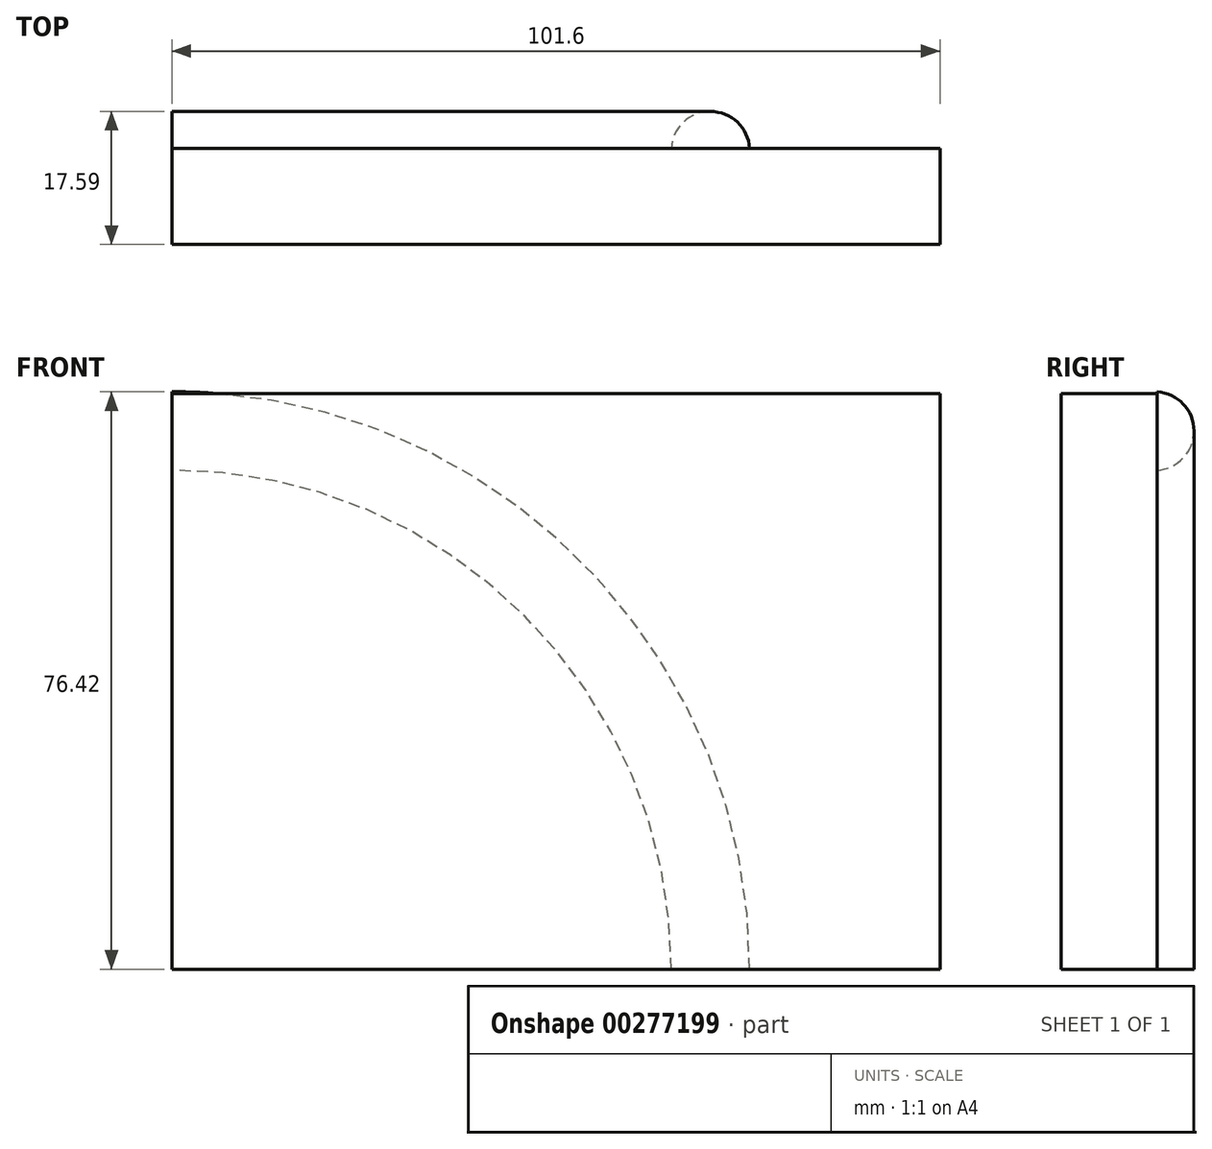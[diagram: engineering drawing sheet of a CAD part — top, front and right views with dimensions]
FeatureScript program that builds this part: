
annotation { "Feature Type Name" : "Feature", "Feature Type Description" : "" }
export const myFeature = defineFeature(function(context is Context, id is Id, definition is map)
    precondition{}
    {
        {
            var Q0;
            Q0=qCreatedBy(makeId("Front.planeOp"),FACE);
            var sketch = newSketch(context, id + "F0", { "sketchPlane" : qUnion([Q0])});
            skLineSegment(sketch, "E0.bottom", {"start": v(0, 0) * mm, "end": v(101.6, 0) * mm});
            skLineSegment(sketch, "E0.top", {"start": v(0, 76.2) * mm, "end": v(101.6, 76.2) * mm});
            skLineSegment(sketch, "E0.left", {"start": v(0, 0) * mm, "end": v(0, 76.2) * mm});
            skLineSegment(sketch, "E0.right", {"start": v(101.6, 0) * mm, "end": v(101.6, 76.2) * mm});
            skArc(sketch, "E1", {"start": v(0, 76.2) * mm, "mid": v(53.88, 53.88) * mm, "end": v(76.2, 0) * mm});
            skArc(sketch, "E2", {"start": v(71.12, 0) * mm, "mid": v(76.2, 5.08) * mm, "end": v(81.28, 0) * mm});
            skSolve(sketch);
        }
        {
            var Q0;
            Q0=makeQuery(id+"F0.imprint","IMPRINT",FACE,{"disambiguationData":[TD([[makeQuery(id+"F0.imprint","IMPRINT",EDGE,{"derivedFrom":sQuery(id+"F0.wireOp",EDGE,"E0.bottom")}),1.0]])]});
            var Q1;
            Q1=makeQuery(id+"F0.imprint","IMPRINT",FACE,{"disambiguationData":[TD([[makeQuery(id+"F0.imprint","IMPRINT",EDGE,{"derivedFrom":sQuery(id+"F0.wireOp",EDGE,"E0.top")}),-1.0]])]});
            var Q2;
            {var subQ0=sQuery(id+"F0.wireOp",EDGE,"E0.left");Q2=makeQuery(id+"F0.imprint","IMPRINT",FACE,{"disambiguationData":[TD([[makeQuery(id+"F0.imprint","IMPRINT",EDGE,{"derivedFrom":subQ0}),-1.0]])]});}
            extrude(context, id + "F1", {"entities" : qUnion([Q0, Q1, Q2]), "depth" : 12.7 * mm});
        }
        {
            var Q0;
            Q0=qCreatedBy(makeId("Top.planeOp"),FACE);
            var sketch = newSketch(context, id + "F2", { "sketchPlane" : qUnion([Q0])});
            skPoint(sketch, "E3", {"position": v(79.24, 0) * mm});
            skPoint(sketch, "E4", {"position": v(66.04, 0) * mm});
            skLineSegment(sketch, "E5", {"start": v(66.04, 0) * mm, "end": v(76.42, 0) * mm});
            skArc(sketch, "E6", {"start": v(76.42, 0) * mm, "mid": v(71.23, 4.89) * mm, "end": v(66.04, 0) * mm});
            skSolve(sketch);
        }
        {
            var Q0;
            Q0=makeQuery(id+"F2.imprint","IMPRINT",FACE,{"disambiguationData":[TD([[makeQuery(id+"F2.imprint","IMPRINT",EDGE,{"derivedFrom":sQuery(id+"F2.wireOp",EDGE,"E5")}),1.0]])]});
            var Q1;
            Q1=sQuery(id+"F0.wireOp",EDGE,"E1");
            sweep(context, id + "F3", {"operationType" : NewBodyOperationType.ADD, "profiles" : qUnion([Q0]), "path" : qUnion([Q1])});
        }
    });
